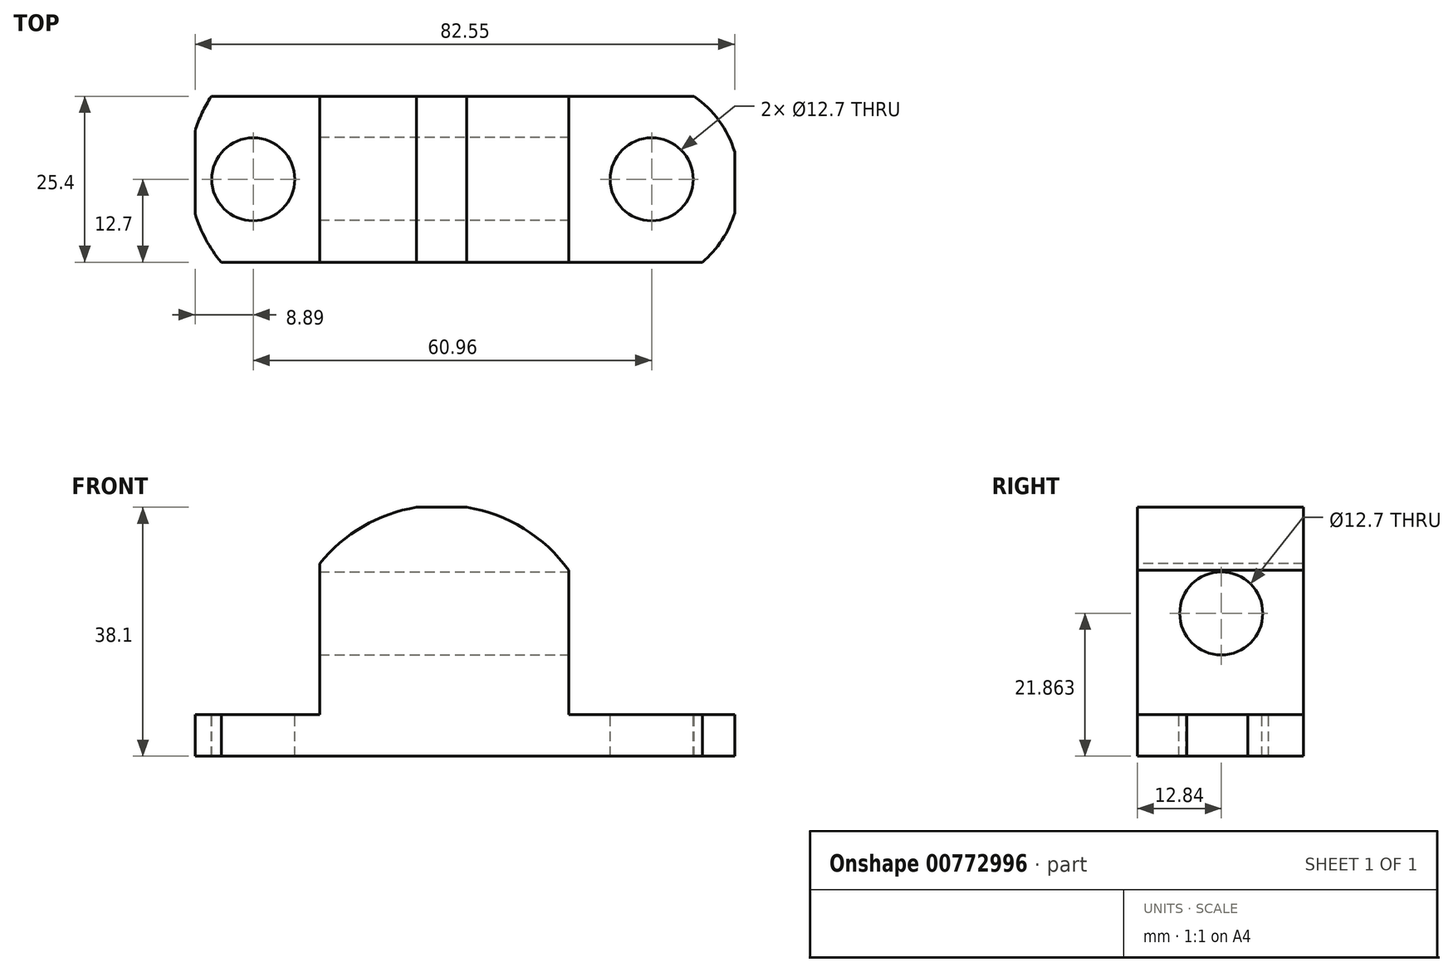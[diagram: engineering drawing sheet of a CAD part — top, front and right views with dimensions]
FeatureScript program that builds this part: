
annotation { "Feature Type Name" : "Feature", "Feature Type Description" : "" }
export const myFeature = defineFeature(function(context is Context, id is Id, definition is map)
    precondition{}
    {
        {
            var Q0;
            Q0=qCreatedBy(makeId("Front.planeOp"),FACE);
            var sketch = newSketch(context, id + "F0", { "sketchPlane" : qUnion([Q0])});
            skLineSegment(sketch, "E0", {"start": v(0, 0) * mm, "end": v(0, 38.1) * mm});
            skLineSegment(sketch, "E1", {"start": v(0, 38.1) * mm, "end": v(82.55, 38.1) * mm});
            skLineSegment(sketch, "E2", {"start": v(82.55, 38.1) * mm, "end": v(82.55, 0) * mm});
            skLineSegment(sketch, "E3", {"start": v(82.55, 0) * mm, "end": v(0, 0) * mm});
            skSolve(sketch);
        }
        {
            var Q0;
            Q0=makeQuery(id+"F0.imprint","IMPRINT",FACE,{"disambiguationData":[TD([[makeQuery(id+"F0.imprint","IMPRINT",EDGE,{"derivedFrom":sQuery(id+"F0.wireOp",EDGE,"E0")}),-1.0]])]});
            var sketch = newSketch(context, id + "F1", { "sketchPlane" : qUnion([Q0])});
            skSolve(sketch);
        }
        {
            var Q0;
            Q0 = qSketchRegion(id + "F0", true);
            extrude(context, id + "F2", {"entities" : qUnion([Q0]), "depth" : 25.4 * mm, "offsetDistance" : 25.4 * mm});
        }
        {
            var Q0;
            Q0=makeQuery(id+"F2.opExtrude","CAP_FACE",FACE,{"disambiguationData":[OSD([sQuery(id+"F0.wireOp",EDGE,"E0"),sQuery(id+"F0.wireOp",EDGE,"E1"),sQuery(id+"F0.wireOp",EDGE,"E2"),sQuery(id+"F0.wireOp",EDGE,"E3")])],"isStart":false});
            var sketch = newSketch(context, id + "F3", { "sketchPlane" : qUnion([Q0])});
            skLineSegment(sketch, "E4", {"start": v(44.45, 38.1) * mm, "end": v(44.45, -12.7) * mm});
            skLineSegment(sketch, "E5", {"start": v(44.45, -12.7) * mm, "end": v(82.55, -12.7) * mm});
            skLineSegment(sketch, "E6", {"start": v(82.55, -12.7) * mm, "end": v(82.55, 38.1) * mm});
            skLineSegment(sketch, "E7", {"start": v(82.55, 38.1) * mm, "end": v(44.45, 38.1) * mm});
            skSolve(sketch);
        }
        {
            var Q0;
            Q0=makeQuery(id+"F3.imprint","IMPRINT",FACE,{"disambiguationData":[TD([[makeQuery(id+"F3.imprint","IMPRINT",EDGE,{"derivedFrom":sQuery(id+"F3.wireOp",EDGE,"E4")}),1.0]])]});
            extrude(context, id + "F4", {"entities" : qUnion([Q0]), "operationType" : NewBodyOperationType.REMOVE, "oppositeDirection" : true, "depth" : 25.4 * mm, "offsetDistance" : 25.4 * mm});
        }
        {
            var Q0;
            Q0=makeQuery(id+"F2.opExtrude","CAP_FACE",FACE,{"disambiguationData":[OSD([sQuery(id+"F0.wireOp",EDGE,"E0"),sQuery(id+"F0.wireOp",EDGE,"E1"),sQuery(id+"F0.wireOp",EDGE,"E2"),sQuery(id+"F0.wireOp",EDGE,"E3")])],"isStart":false});
            var sketch = newSketch(context, id + "F5", { "sketchPlane" : qUnion([Q0])});
            skLineSegment(sketch, "E8", {"start": v(19.05, 38.1) * mm, "end": v(19.05, -12.7) * mm});
            skLineSegment(sketch, "E9", {"start": v(19.05, -12.7) * mm, "end": v(0, -12.7) * mm});
            skLineSegment(sketch, "E10", {"start": v(0, -12.7) * mm, "end": v(0, 38.1) * mm});
            skLineSegment(sketch, "E11", {"start": v(0, 38.1) * mm, "end": v(19.05, 38.1) * mm});
            skSolve(sketch);
        }
        {
            var Q0;
            Q0 = qSketchRegion(id + "F3", true);
            var Q1;
            Q1=makeQuery(id+"F1.imprint","IMPRINT",FACE,{"disambiguationData":[TD([[makeQuery(id+"F1.imprint","IMPRINT",EDGE,{"derivedFrom":makeQuery(id+"F0.imprint","IMPRINT",EDGE,{"derivedFrom":sQuery(id+"F0.wireOp",EDGE,"E0")})}),-1.0]])]});
            extrude(context, id + "F6", {"entities" : qUnion([Q0, Q1]), "operationType" : NewBodyOperationType.REMOVE, "oppositeDirection" : true, "depth" : 25.4 * mm, "offsetDistance" : 25.4 * mm});
        }
        {
            var Q0;
            Q0 = qSketchRegion(id + "F5", true);
            extrude(context, id + "F7", {"entities" : qUnion([Q0]), "operationType" : NewBodyOperationType.REMOVE, "oppositeDirection" : true, "depth" : 25.4 * mm, "offsetDistance" : 25.4 * mm});
        }
        {
            var Q0;
            Q0 = qSketchRegion(id + "F0", true);
            extrude(context, id + "F8", {"entities" : qUnion([Q0]), "operationType" : NewBodyOperationType.ADD, "depth" : 25.4 * mm, "offsetDistance" : 25.4 * mm});
        }
        {
            var Q0;
            {var subQ0=sQuery(id+"F0.wireOp",EDGE,"E3");var subQ1=sQuery(id+"F0.wireOp",EDGE,"E2");var subQ2=sQuery(id+"F0.wireOp",EDGE,"E1");var subQ3=sQuery(id+"F0.wireOp",EDGE,"E0");Q0=makeQuery(id+"F8.boolean.opBoolean","MERGE",FACE,{"derivedFrom":[makeQuery(id+"F2.opExtrude","CAP_FACE",FACE,{"disambiguationData":[OSD([subQ3,subQ2,subQ1,subQ0])],"isStart":false}),makeQuery(id+"F8.opExtrude","CAP_FACE",FACE,{"disambiguationData":[OSD([subQ3,subQ2,subQ1,subQ0])],"isStart":false})]});}
            var sketch = newSketch(context, id + "F9", { "sketchPlane" : qUnion([Q0])});
            skLineSegment(sketch, "E12", {"start": v(57.15, 38.1) * mm, "end": v(57.15, 6.35) * mm});
            skLineSegment(sketch, "E13", {"start": v(57.15, 6.35) * mm, "end": v(82.55, 6.35) * mm});
            skLineSegment(sketch, "E14", {"start": v(82.55, 6.35) * mm, "end": v(82.55, 38.1) * mm});
            skLineSegment(sketch, "E15", {"start": v(82.55, 38.1) * mm, "end": v(57.15, 38.1) * mm});
            skSolve(sketch);
        }
        {
            var Q0;
            Q0 = qSketchRegion(id + "F9", true);
            extrude(context, id + "F10", {"entities" : qUnion([Q0]), "operationType" : NewBodyOperationType.REMOVE, "oppositeDirection" : true, "depth" : 25.4 * mm, "offsetDistance" : 25.4 * mm});
        }
        {
            var Q0;
            {var subQ0=sQuery(id+"F0.wireOp",EDGE,"E3");var subQ1=sQuery(id+"F0.wireOp",EDGE,"E2");var subQ2=sQuery(id+"F0.wireOp",EDGE,"E1");var subQ3=sQuery(id+"F0.wireOp",EDGE,"E0");Q0=makeQuery(id+"F8.boolean.opBoolean","MERGE",FACE,{"derivedFrom":[makeQuery(id+"F2.opExtrude","CAP_FACE",FACE,{"disambiguationData":[OSD([subQ3,subQ2,subQ1,subQ0])],"isStart":false}),makeQuery(id+"F8.opExtrude","CAP_FACE",FACE,{"disambiguationData":[OSD([subQ3,subQ2,subQ1,subQ0])],"isStart":false})]});}
            var sketch = newSketch(context, id + "F11", { "sketchPlane" : qUnion([Q0])});
            skLineSegment(sketch, "E16", {"start": v(19.05, 38.1) * mm, "end": v(19.05, 6.35) * mm});
            skLineSegment(sketch, "E17", {"start": v(19.05, 6.35) * mm, "end": v(0, 6.35) * mm});
            skLineSegment(sketch, "E18", {"start": v(0, 6.35) * mm, "end": v(0, 38.1) * mm});
            skLineSegment(sketch, "E19", {"start": v(0, 38.1) * mm, "end": v(19.05, 38.1) * mm});
            skSolve(sketch);
        }
        {
            var Q0;
            Q0=makeQuery(id+"F11.imprint","IMPRINT",FACE,{"disambiguationData":[TD([[makeQuery(id+"F11.imprint","IMPRINT",EDGE,{"derivedFrom":sQuery(id+"F11.wireOp",EDGE,"E16")}),-1.0]])]});
            extrude(context, id + "F12", {"entities" : qUnion([Q0]), "operationType" : NewBodyOperationType.REMOVE, "oppositeDirection" : true, "depth" : 25.4 * mm, "offsetDistance" : 25.4 * mm});
        }
        {
            var Q0;
            Q0=makeQuery(id+"F10.boolean.opBoolean","COPY",FACE,{"derivedFrom":makeQuery(id+"F10.opExtrude","SWEPT_FACE",FACE,{"disambiguationData":[OSD([sQuery(id+"F9.wireOp",EDGE,"E13")])]})});
            var sketch = newSketch(context, id + "F13", { "sketchPlane" : qUnion([Q0])});
            skCircle(sketch, "E20", {"center": v(69.85, -12.7) * mm, "radius": 6.35 * mm});
            skPoint(sketch, "E20.centerSnap0", {"position": v(82.55, -12.7) * mm});
            skSolve(sketch);
        }
        {
            var Q0;
            Q0=makeQuery(id+"F13.imprint","IMPRINT",FACE,{"disambiguationData":[TD([[makeQuery(id+"F13.imprint","IMPRINT",EDGE,{"derivedFrom":sQuery(id+"F13.wireOp",EDGE,"E20")}),1.0]])]});
            extrude(context, id + "F14", {"entities" : qUnion([Q0]), "operationType" : NewBodyOperationType.REMOVE, "oppositeDirection" : true, "depth" : 25.4 * mm, "offsetDistance" : 25.4 * mm});
        }
        {
            var Q0;
            Q0=makeQuery(id+"F12.boolean.opBoolean","COPY",FACE,{"derivedFrom":makeQuery(id+"F12.opExtrude","SWEPT_FACE",FACE,{"disambiguationData":[OSD([sQuery(id+"F11.wireOp",EDGE,"E17")])]})});
            var sketch = newSketch(context, id + "F15", { "sketchPlane" : qUnion([Q0])});
            skCircle(sketch, "E21", {"center": v(8.9, -12.7) * mm, "radius": 6.35 * mm});
            skPoint(sketch, "E21.centerSnap0", {"position": v(19.05, -12.7) * mm});
            skSolve(sketch);
        }
        {
            var Q0;
            Q0=makeQuery(id+"F15.imprint","IMPRINT",FACE,{"disambiguationData":[TD([[makeQuery(id+"F15.imprint","IMPRINT",EDGE,{"derivedFrom":sQuery(id+"F15.wireOp",EDGE,"E21")}),1.0]])]});
            extrude(context, id + "F16", {"entities" : qUnion([Q0]), "operationType" : NewBodyOperationType.REMOVE, "oppositeDirection" : true, "depth" : 25.4 * mm, "offsetDistance" : 25.4 * mm});
        }
        {
            var Q0;
            Q0=makeQuery(id+"F10.boolean.opBoolean","COPY",FACE,{"derivedFrom":makeQuery(id+"F10.opExtrude","SWEPT_FACE",FACE,{"disambiguationData":[OSD([sQuery(id+"F9.wireOp",EDGE,"E12")])]})});
            var sketch = newSketch(context, id + "F17", { "sketchPlane" : qUnion([Q0])});
            skCircle(sketch, "E22", {"center": v(-12.56, 21.86) * mm, "radius": 6.35 * mm});
            skSolve(sketch);
        }
        {
            var Q0;
            Q0=makeQuery(id+"F17.imprint","IMPRINT",FACE,{"disambiguationData":[TD([[makeQuery(id+"F17.imprint","IMPRINT",EDGE,{"derivedFrom":sQuery(id+"F17.wireOp",EDGE,"E22")}),1.0]])]});
            extrude(context, id + "F18", {"entities" : qUnion([Q0]), "operationType" : NewBodyOperationType.REMOVE, "oppositeDirection" : true, "depth" : 25.4 * mm, "offsetDistance" : 25.4 * mm});
        }
        {
            var Q0;
            Q0=makeQuery(id+"F18.boolean.opBoolean","COPY",FACE,{"derivedFrom":makeQuery(id+"F18.opExtrude","CAP_FACE",FACE,{"disambiguationData":[OSD([sQuery(id+"F17.wireOp",EDGE,"E22")])],"isStart":false})});
            var sketch = newSketch(context, id + "F19", { "sketchPlane" : qUnion([Q0])});
            skSolve(sketch);
        }
        {
            var Q0;
            Q0 = qSketchRegion(id + "F19", true);
            var Q1;
            Q1=makeQuery(id+"F19.imprint","IMPRINT",FACE,{"disambiguationData":[TD([[makeQuery(id+"F19.imprint","IMPRINT",EDGE,{"derivedFrom":makeQuery(id+"F18.boolean.opBoolean","COPY",EDGE,{"derivedFrom":makeQuery(id+"F18.opExtrude","CAP_EDGE",EDGE,{"disambiguationData":[OSD([sQuery(id+"F17.wireOp",EDGE,"E22")])],"isStart":false})})}),1.0]])]});
            extrude(context, id + "F20", {"entities" : qUnion([Q0, Q1]), "operationType" : NewBodyOperationType.REMOVE, "oppositeDirection" : true, "depth" : 50.8 * mm, "offsetDistance" : 25.4 * mm});
        }
        {
            var Q0;
            {var subQ0=sQuery(id+"F0.wireOp",EDGE,"E3");var subQ1=sQuery(id+"F0.wireOp",EDGE,"E2");var subQ2=sQuery(id+"F0.wireOp",EDGE,"E1");var subQ3=sQuery(id+"F0.wireOp",EDGE,"E0");Q0=makeQuery(id+"F8.boolean.opBoolean","MERGE",FACE,{"derivedFrom":[makeQuery(id+"F2.opExtrude","CAP_FACE",FACE,{"disambiguationData":[OSD([subQ3,subQ2,subQ1,subQ0])],"isStart":false}),makeQuery(id+"F8.opExtrude","CAP_FACE",FACE,{"disambiguationData":[OSD([subQ3,subQ2,subQ1,subQ0])],"isStart":false})]});}
            var sketch = newSketch(context, id + "F21", { "sketchPlane" : qUnion([Q0])});
            skArc(sketch, "E23", {"start": v(57.15, 28.47) * mm, "mid": v(38.35, 38.4) * mm, "end": v(19.05, 29.47) * mm});
            skLineSegment(sketch, "E24", {"start": v(57.15, 28.47) * mm, "end": v(57.15, 38.1) * mm});
            skLineSegment(sketch, "E25", {"start": v(57.15, 38.1) * mm, "end": v(19.05, 38.1) * mm});
            skLineSegment(sketch, "E26", {"start": v(19.05, 38.1) * mm, "end": v(19.05, 29.47) * mm});
            skSolve(sketch);
        }
        {
            var Q0;
            Q0 = qSketchRegion(id + "F21", true);
            extrude(context, id + "F22", {"entities" : qUnion([Q0]), "operationType" : NewBodyOperationType.REMOVE, "oppositeDirection" : true, "depth" : 25.4 * mm, "offsetDistance" : 25.4 * mm});
        }
        {
            var Q0;
            Q0=makeQuery(id+"F10.boolean.opBoolean","COPY",FACE,{"derivedFrom":makeQuery(id+"F10.opExtrude","SWEPT_FACE",FACE,{"disambiguationData":[OSD([sQuery(id+"F9.wireOp",EDGE,"E13")])]})});
            var sketch = newSketch(context, id + "F23", { "sketchPlane" : qUnion([Q0])});
            skArc(sketch, "E27", {"start": v(77.58, -25.4) * mm, "mid": v(83.22, -12.4) * mm, "end": v(76.33, 0) * mm});
            skArc(sketch, "E28", {"start": v(3.35, 0) * mm, "mid": v(-0.4, -12.7) * mm, "end": v(3.39, -25.4) * mm});
            skSolve(sketch);
        }
        {
            var Q0;
            {var subQ0=sQuery(id+"F23.wireOp",EDGE,"E27");var subQ1=sQuery(id+"F9.wireOp",EDGE,"E13");var subQ2=makeQuery(id+"F10.boolean.opBoolean","COPY",EDGE,{"derivedFrom":makeQuery(id+"F10.opExtrude","CAP_EDGE",EDGE,{"disambiguationData":[OSD([subQ1])],"isStart":false})});var subQ3=makeQuery(id+"F23.imprint","INTERSECT",VERTEX,{"derivedFrom":[subQ2,subQ0]});Q0=makeQuery(id+"F23.imprint","IMPRINT",FACE,{"disambiguationData":[TD([[makeQuery(id+"F23.imprint","IMPRINT",EDGE,{"disambiguationData":[TD([[subQ3,1.0]])],"derivedFrom":subQ0}),-1.0]])]});}
            var Q1;
            {var subQ0=sQuery(id+"F23.wireOp",EDGE,"E27");var subQ1=sQuery(id+"F9.wireOp",EDGE,"E13");var subQ2=makeQuery(id+"F10.boolean.opBoolean","COPY",EDGE,{"derivedFrom":makeQuery(id+"F10.opExtrude","CAP_EDGE",EDGE,{"disambiguationData":[OSD([subQ1])],"isStart":true})});var subQ3=makeQuery(id+"F23.imprint","INTERSECT",VERTEX,{"derivedFrom":[subQ2,subQ0]});Q1=makeQuery(id+"F23.imprint","IMPRINT",FACE,{"disambiguationData":[TD([[makeQuery(id+"F23.imprint","IMPRINT",EDGE,{"disambiguationData":[TD([[subQ3,-1.0]])],"derivedFrom":subQ0}),-1.0]])]});}
            extrude(context, id + "F24", {"entities" : qUnion([Q0, Q1]), "operationType" : NewBodyOperationType.REMOVE, "oppositeDirection" : true, "depth" : 25.4 * mm, "offsetDistance" : 25.4 * mm});
        }
        {
            var Q0;
            Q0=makeQuery(id+"F12.boolean.opBoolean","COPY",FACE,{"derivedFrom":makeQuery(id+"F12.opExtrude","SWEPT_FACE",FACE,{"disambiguationData":[OSD([sQuery(id+"F11.wireOp",EDGE,"E17")])]})});
            var sketch = newSketch(context, id + "F25", { "sketchPlane" : qUnion([Q0])});
            skArc(sketch, "E29", {"start": v(2.46, 0) * mm, "mid": v(-0.9, -12.95) * mm, "end": v(4, -25.4) * mm});
            skSolve(sketch);
        }
        {
            var Q0;
            Q0 = qSketchRegion(id + "F25", true);
            var Q1;
            {var subQ0=sQuery(id+"F25.wireOp",EDGE,"E29");var subQ1=sQuery(id+"F11.wireOp",EDGE,"E17");var subQ2=makeQuery(id+"F12.boolean.opBoolean","COPY",EDGE,{"derivedFrom":makeQuery(id+"F12.opExtrude","CAP_EDGE",EDGE,{"disambiguationData":[OSD([subQ1])],"isStart":false})});var subQ3=makeQuery(id+"F25.imprint","INTERSECT",VERTEX,{"derivedFrom":[subQ2,subQ0]});Q1=makeQuery(id+"F25.imprint","IMPRINT",FACE,{"disambiguationData":[TD([[makeQuery(id+"F25.imprint","IMPRINT",EDGE,{"disambiguationData":[TD([[subQ3,-1.0]])],"derivedFrom":subQ0}),-1.0]])]});}
            var Q2;
            {var subQ0=sQuery(id+"F25.wireOp",EDGE,"E29");var subQ1=sQuery(id+"F11.wireOp",EDGE,"E17");var subQ2=makeQuery(id+"F12.boolean.opBoolean","COPY",EDGE,{"derivedFrom":makeQuery(id+"F12.opExtrude","CAP_EDGE",EDGE,{"disambiguationData":[OSD([subQ1])],"isStart":true})});var subQ3=makeQuery(id+"F25.imprint","INTERSECT",VERTEX,{"derivedFrom":[subQ2,subQ0]});Q2=makeQuery(id+"F25.imprint","IMPRINT",FACE,{"disambiguationData":[TD([[makeQuery(id+"F25.imprint","IMPRINT",EDGE,{"disambiguationData":[TD([[subQ3,1.0]])],"derivedFrom":subQ0}),-1.0]])]});}
            extrude(context, id + "F26", {"entities" : qUnion([Q0, Q1, Q2]), "operationType" : NewBodyOperationType.REMOVE, "oppositeDirection" : true, "depth" : 25.4 * mm, "offsetDistance" : 25.4 * mm});
        }
    });
